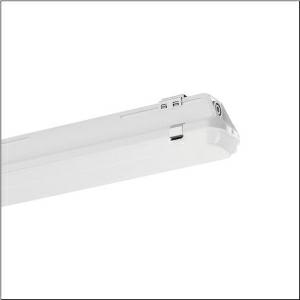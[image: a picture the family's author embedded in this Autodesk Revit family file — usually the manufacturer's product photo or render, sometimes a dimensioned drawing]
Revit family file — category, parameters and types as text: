
# Revit family: monsun_r__11_51fp12mp480h_cfdd
name_source: partatom
category: Lighting Fixtures
units: mm (PartAtom-declared; Revit-internal decimal feet)

## family parameters
Cut with Voids When Loaded = No
Host = Face
Light Source = No
Part Type = Normal
Room Calculation Point = No
Round Connector Dimension = Use Diameter
Shared = No

## types (1)
- --- (1 x LED, 7990 lm, 45.4 W, 4000K)
    Apparent Load = 45 VA
    CIE Flux Codes = 65 88 97 97 100
    Color Rendering = 80
    Color Temperature = 4000K
    Default Elevation = 1800 mm
    Description = Monsun® 11, damp-proof luminaire, chain hanger, primary light control with lens, primary optical cover: enclosure, of PMMA, light emission: direct distribution, primary light characteristic: symmetric, installation type: suspended mounting, surface-mounted, horizontal mounting, vertical mounting, LED, rated luminous flux: 7.990lm, luminous efficacy: 176lm/W, light colour: 840, colour temperature: 4000K, control gear: ON/OFF Multilumen, with terminal, 3-pole, max. 2.5mm², mains connection: 220..240V, AC, 50/60Hz, rated input power: 45W, luminaire housing, of glass-fibre reinforced polyester, uncoated, bright grey, incl. chain hanger, length: 1.590mm, width: 90mm, height: 88mm, clip for enclosure, of stainless steel (V2A), ceiling mounting element, of stainless steel (V2A), chain hanger, of stainless steel (V2A), protection rating (complete): IP66, insulation class (complete): insulation class I (protective earthing), certification: CE, ENEC, VDE, UKCA, protection symbol: D, impact resistance: IK04, permissible operating ambient temperature: -35..+40°C, standard: EN 50419, EN 60598-2-1, no direct snow, no direct sun, no direct rain, for indoor or canopied outdoor use, corresponds to IFS (International Featured Standards) requirements for safety and quality in the food industry, contact your sales advisor before using the luminaires in applications with unclear chemical exposure, large temperature fluctuations or condensation-forming humidity, LABS conformity tested according to VDMA 24364:2018-05, packaging unit: 1 piece
    Height = 89 mm
    Lamp = 1 x LED
    Lamp Light Flux = 7990 lm
    Lamp Power = 45.4 W
    Lamp count = 1
    Length = 1590 mm
    Luminous efficacy = 176 lm/W
    Manufacturer = Siteco
    ModVariant = No
    Model = 51FP12MP480H
    Mounting Place = Ceiling
    Mounting Type = Surface mounted
    Number of Poles = 1
    OnlyDefault = Yes
    Power Factor = 1
    Product Name = Monsun® 11
    Product group = damp-proof luminaire
    ProductGroupID = 300
    Protection Class = Protection class I
    Protection Degree = IP 66
    RLX_Detail_Level = 1
    RLX_Emergency_Light_Flux = 0 lm
    RLX_Emergency_Type = 0
    RLX_Emergency_Type_DB = No
    RlxData = <blob elided: 89785 chars, md5=2cf18de6>
    Socket = socket
    Standby Power = 0 W
    System Light Flux = 7990 lm
    System Power = 45 W
    Type Comments = factory setting: luminous flux: 100 % | (A | C | E) | 105 mA
    Type Image = l_1349237.jpg
    URL = http://relux.com
    VarID = @adj_199718
    Voltage = 0 V
    Weight = 0.00 kg
    Width = 90 mm

## geometry (parser evidence)
native form markers: Blend x4, Sweep x10
no freeform markers — native parametric forms only
